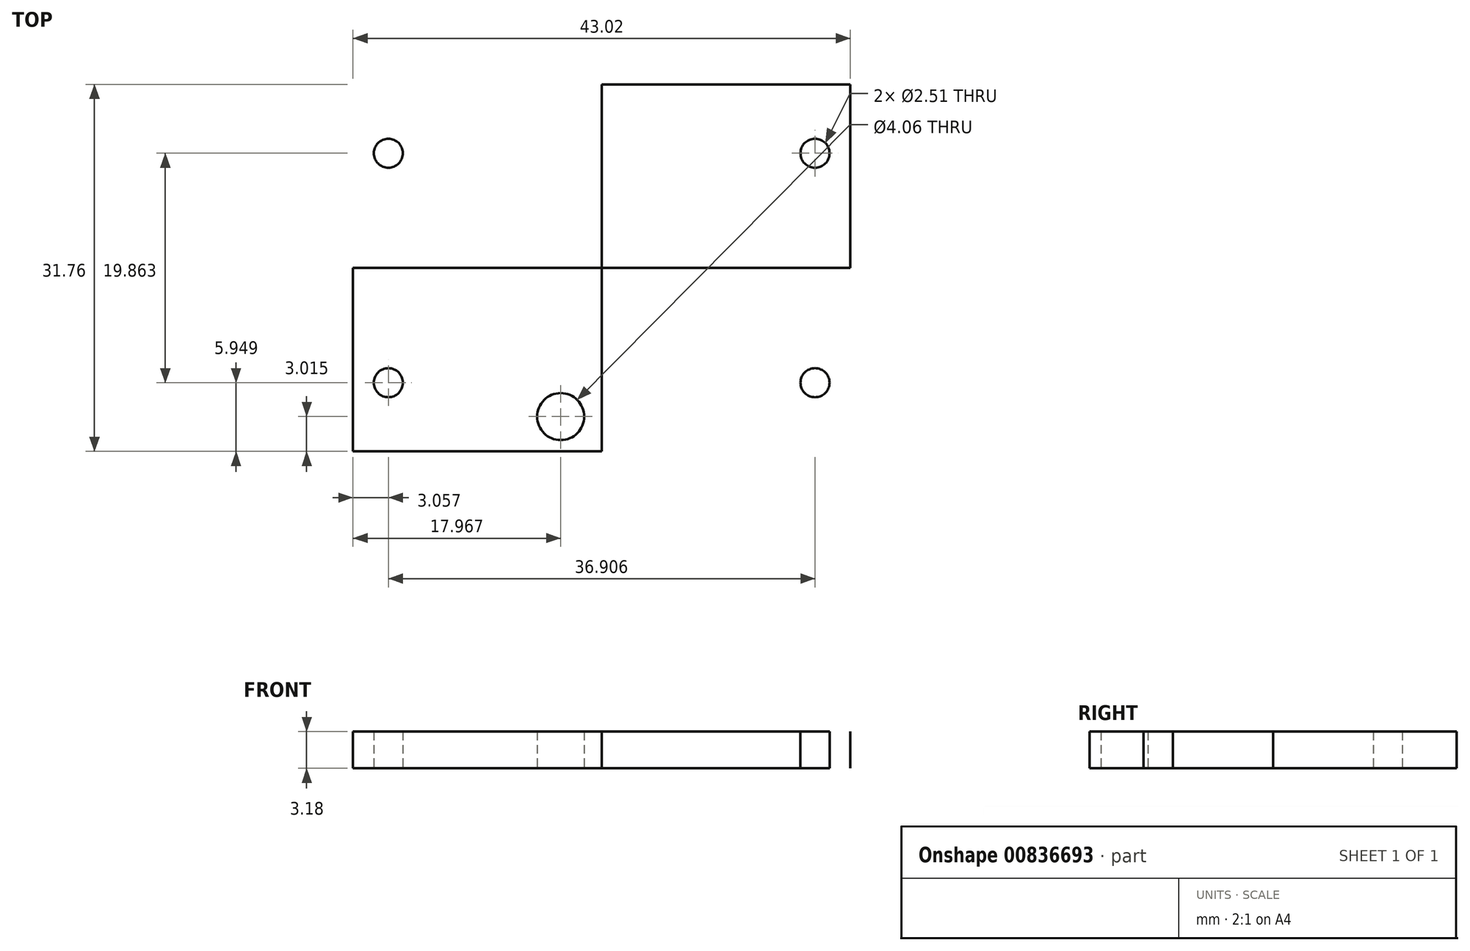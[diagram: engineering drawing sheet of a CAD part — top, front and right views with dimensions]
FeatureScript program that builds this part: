
annotation { "Feature Type Name" : "Feature", "Feature Type Description" : "" }
export const myFeature = defineFeature(function(context is Context, id is Id, definition is map)
    precondition{}
    {
        {
            var Q0;
            Q0=qCreatedBy(makeId("Top.planeOp"),FACE);
            var sketch = newSketch(context, id + "F0", { "sketchPlane" : qUnion([Q0])});
            skLineSegment(sketch, "E0.bottom", {"start": v(21.51, 15.88) * mm, "end": v(-21.51, 15.88) * mm});
            skLineSegment(sketch, "E0.top", {"start": v(21.51, -15.88) * mm, "end": v(-21.51, -15.88) * mm});
            skLineSegment(sketch, "E0.left", {"start": v(21.51, 15.88) * mm, "end": v(21.51, -15.88) * mm});
            skLineSegment(sketch, "E0.right", {"start": v(-21.51, 15.88) * mm, "end": v(-21.51, -15.88) * mm});
            skPoint(sketch, "E0.middle", {"position": v(0, 0) * mm});
            skCircle(sketch, "E1", {"center": v(18.45, 9.93) * mm, "radius": 1.26 * mm});
            skLineSegment(sketch, "E2", {"start": v(-21.51, 0) * mm, "end": v(21.51, 0) * mm});
            skLineSegment(sketch, "E3", {"start": v(0, 15.88) * mm, "end": v(0, -15.88) * mm});
            skCircle(sketch, "E4.MirrorC", {"center": v(-18.45, 9.93) * mm, "radius": 1.26 * mm});
            skCircle(sketch, "E5.MirrorC", {"center": v(-18.45, -9.93) * mm, "radius": 1.26 * mm});
            skCircle(sketch, "E6.MirrorC", {"center": v(18.45, -9.93) * mm, "radius": 1.26 * mm});
            skCircle(sketch, "E7", {"center": v(-3.54, 12.87) * mm, "radius": 2.03 * mm});
            skCircle(sketch, "E8.MirrorC", {"center": v(-3.54, -12.87) * mm, "radius": 2.03 * mm});
            skSolve(sketch);
        }
        {
            var Q0;
            Q0=makeQuery(id+"F0.imprint","IMPRINT",FACE,{"disambiguationData":[TD([[makeQuery(id+"F0.imprint","IMPRINT",EDGE,{"derivedFrom":sQuery(id+"F0.wireOp",EDGE,"E4.MirrorC")}),1.0]])]});
            var Q1;
            Q1=makeQuery(id+"F0.imprint","IMPRINT",FACE,{"disambiguationData":[TD([[makeQuery(id+"F0.imprint","IMPRINT",EDGE,{"derivedFrom":sQuery(id+"F0.wireOp",EDGE,"E5.MirrorC")}),-1.0]])]});
            var Q2;
            Q2=makeQuery(id+"F0.imprint","IMPRINT",FACE,{"disambiguationData":[TD([[makeQuery(id+"F0.imprint","IMPRINT",EDGE,{"derivedFrom":sQuery(id+"F0.wireOp",EDGE,"E6.MirrorC")}),1.0]])]});
            var Q3;
            Q3=makeQuery(id+"F0.imprint","IMPRINT",FACE,{"disambiguationData":[TD([[makeQuery(id+"F0.imprint","IMPRINT",EDGE,{"derivedFrom":sQuery(id+"F0.wireOp",EDGE,"E1")}),-1.0]])]});
            extrude(context, id + "F1", {"entities" : qUnion([Q0, Q1, Q2, Q3]), "depth" : 3.17 * mm, "offsetDistance" : 25.4 * mm});
        }
    });
